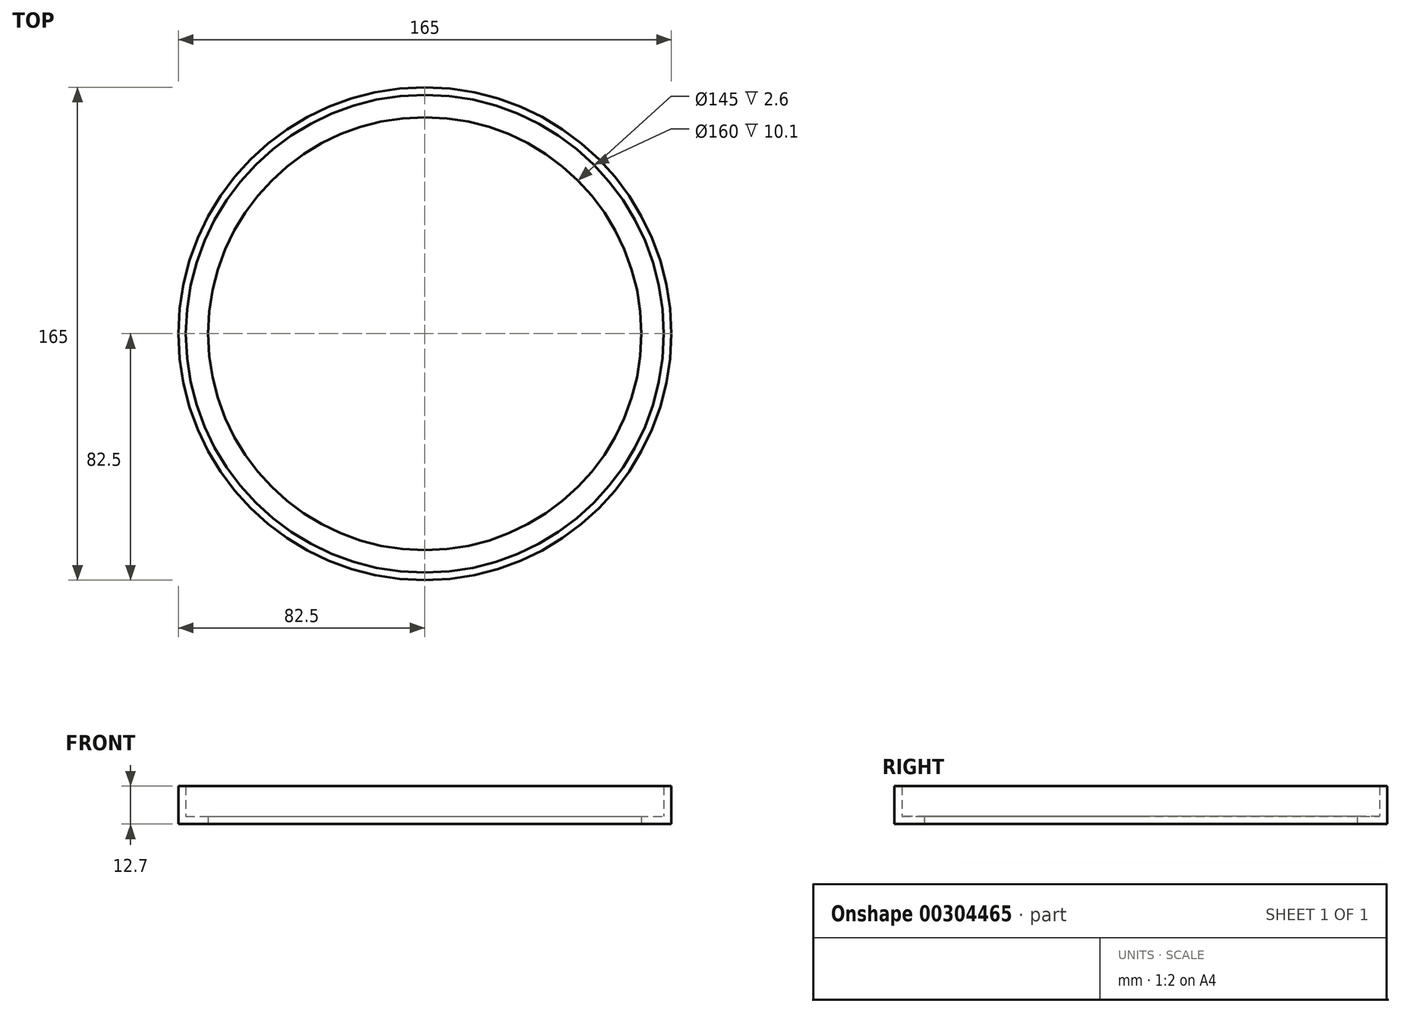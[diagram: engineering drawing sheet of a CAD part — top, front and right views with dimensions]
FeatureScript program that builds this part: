
annotation { "Feature Type Name" : "Feature", "Feature Type Description" : "" }
export const myFeature = defineFeature(function(context is Context, id is Id, definition is map)
    precondition{}
    {
        {
            var Q0;
            Q0=qCreatedBy(makeId("Front.planeOp"),FACE);
            var sketch = newSketch(context, id + "F0", { "sketchPlane" : qUnion([Q0])});
            skLineSegment(sketch, "E0", {"start": v(-86.48, 0) * mm, "end": v(87.74, 0) * mm, "construction": true});
            skLineSegment(sketch, "E1", {"start": v(-82.5, 12.7) * mm, "end": v(-82.5, 0) * mm});
            skLineSegment(sketch, "E2", {"start": v(-82.5, 0) * mm, "end": v(-72.5, 0) * mm});
            skLineSegment(sketch, "E3", {"start": v(-72.5, 0) * mm, "end": v(-72.5, 2.6) * mm});
            skLineSegment(sketch, "E4", {"start": v(-72.5, 2.6) * mm, "end": v(-80, 2.6) * mm});
            skLineSegment(sketch, "E5", {"start": v(-80, 2.6) * mm, "end": v(-80, 12.7) * mm});
            skLineSegment(sketch, "E6", {"start": v(-80, 12.7) * mm, "end": v(-82.5, 12.7) * mm});
            skSolve(sketch);
        }
        {
            var Q0;
            Q0=qCreatedBy(makeId("Top.planeOp"),FACE);
            var sketch = newSketch(context, id + "F1", { "sketchPlane" : qUnion([Q0])});
            skCircle(sketch, "E7", {"center": v(0, 0) * mm, "radius": 72.5 * mm, "construction": true});
            skSolve(sketch);
        }
        {
            var Q0;
            Q0 = qSketchRegion(id + "F0", true);
            var Q1;
            Q1=sQuery(id+"F1.wireOp",EDGE,"E7");
            revolve(context, id + "F2", {"entities" : qUnion([Q0]), "axis" : qUnion([Q1]), "revolveType" : RevolveType.FULL});
        }
    });
